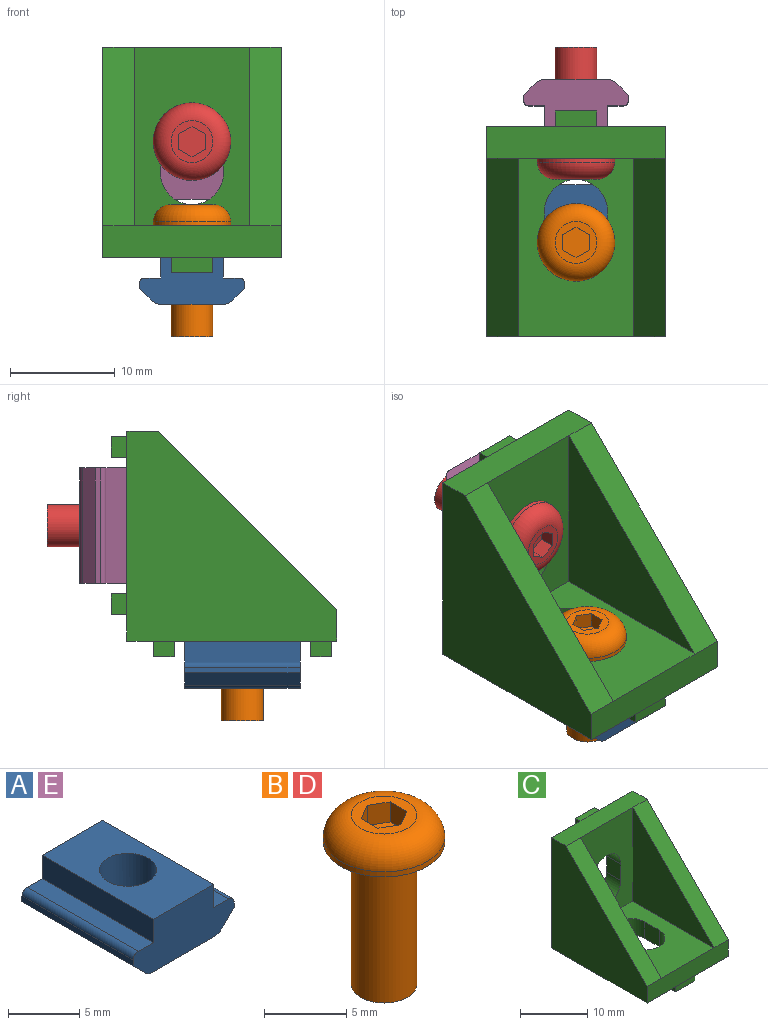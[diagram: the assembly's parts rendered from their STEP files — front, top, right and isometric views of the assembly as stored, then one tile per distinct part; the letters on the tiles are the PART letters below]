
ASSEMBLY  parts=5 mates=4
PART A: 17 faces, bbox 10x11x4.5 mm
  f0: plane 11x1.21mm, normal (-0.71,0,-0.71), area 18.8mm2, adj f1,f13,f14,f15
  f1: cylinder r=1mm len=11mm, axis (0,1,0), area 8.6mm2, adj f0,f2,f14,f15
  f2: plane 11x6.17mm, normal (0,0,-1), area 55.3mm2, adj f1,f3,f14,f15,f16
  f3: cylinder r=1mm len=11mm, axis (0,1,0), area 8.6mm2, adj f2,f4,f14,f15
  f4: plane 11x1.21mm, normal (0.71,0,-0.71), area 18.8mm2, adj f3,f5,f14,f15
  f5: plane 11x0.5mm, normal (1,0,0), area 5.5mm2, adj f4,f6,f14,f15
  f6: cylinder r=0.5mm len=11mm, axis (0,1,0), area 8.6mm2, adj f5,f7,f14,f15
  f7: plane 11x1.5mm, normal (0,0,1), area 16.5mm2, adj f6,f8,f14,f15
  f8: plane 11x2mm, normal (1,0,0), area 22mm2, adj f7,f9,f14,f15
  f9: plane 11x6mm, normal (0,0,1), area 53.4mm2, adj f8,f10,f14,f15,f16
  f10: plane 11x2mm, normal (-1,0,0), area 22mm2, adj f9,f11,f14,f15
  f11: plane 11x1.5mm, normal (0,0,1), area 16.5mm2, adj f10,f12,f14,f15
  f12: cylinder r=0.5mm len=11mm, axis (0,1,0), area 8.6mm2, adj f11,f13,f14,f15
  f13: plane 11x0.5mm, normal (-1,0,0), area 5.5mm2, adj f0,f12,f14,f15
  f14: plane 10x4.5mm, normal (0,-1,0), area 34.6mm2, adj f0,f1,f2,f3,f4,f5,f6,f7
  f15: plane 10x4.5mm, normal (0,1,0), area 34.6mm2, adj f0,f1,f2,f3,f4,f5,f6,f7
  f16: cylinder r=2mm len=4.5mm, axis (0,0,1), area 56.5mm2, adj f2,f9
PART B: 14 faces, bbox 8x8x12.6 mm
  f0: plane 4x4mm, normal (0,0,1), area 7.2mm2, adj f5,f6,f7,f8,f9,f10,f11
  f1: cylinder r=2mm len=10.4mm, axis (0,0,1), area 130.7mm2, adj f2,f13
  f2: torus R=2.2mm, axis (0,0,1), area 4.1mm2, adj f1,f3
  f3: plane 7.4x7.4mm, normal (0,0,-1), area 27.8mm2, adj f2,f4
  f4: cylinder r=3.7mm len=7.4mm, axis (0,0,1), area 8.8mm2, adj f3,f5
  f5: torus R=2mm, axis (0,0,1), area 49.9mm2, adj f0,f4
  f6: plane 1.5x1.25mm, normal (-0.5,-0.87,0), area 2.2mm2, adj f0,f7,f11,f12
  f7: plane 1.5x1.25mm, normal (0.5,-0.87,0), area 2.2mm2, adj f0,f6,f8,f12
  f8: plane 1.5x1.44mm, normal (1,0,0), area 2.2mm2, adj f0,f7,f9,f12
  f9: plane 1.5x1.25mm, normal (0.5,0.87,0), area 2.2mm2, adj f0,f8,f10,f12
  f10: plane 1.5x1.25mm, normal (-0.5,0.87,0), area 2.2mm2, adj f0,f9,f11,f12
  f11: plane 1.5x1.44mm, normal (-1,0,0), area 2.2mm2, adj f0,f6,f10,f12
  f12: plane 2.89x2.5mm, normal (0,0,1), area 5.4mm2, adj f6,f7,f8,f9,f10,f11
  f13: plane 4x4mm, normal (0,0,-1), area 12.6mm2, adj f1
PART C: 40 faces, bbox 17x21.5x21.5 mm
  f0: plane 17x11mm, normal (0,0,1), area 140.7mm2, adj f1,f3,f5,f6,f7,f8,f17,f19
  f1: plane 17x11mm, normal (0,-1,0), area 140.7mm2, adj f0,f11,f12,f13,f14,f15,f17,f19
  f2: plane 20x20mm, normal (-1,0,0), area 255.5mm2, adj f3,f9,f10,f14,f18
  f3: plane 17x3mm, normal (0,-1,0), area 51mm2, adj f0,f2,f4,f10,f16,f18
  f4: plane 20x20mm, normal (1,0,0), area 255.5mm2, adj f3,f9,f10,f14,f16
  f5: cylinder r=3mm len=6mm, axis (0,0,-1), area 28.3mm2, adj f0,f6,f8,f10
  f6: plane 3x3mm, normal (1,0,0), area 9mm2, adj f0,f5,f7,f10
  f7: cylinder r=3mm len=6mm, axis (0,0,-1), area 28.3mm2, adj f0,f6,f8,f10
  f8: plane 3x3mm, normal (-1,0,0), area 9mm2, adj f0,f5,f7,f10
  f9: plane 20x17mm, normal (0,1,0), area 277.7mm2, adj f2,f4,f10,f11,f12,f13,f14,f15
  f10: plane 20x17mm, normal (0,0,-1), area 277.7mm2, adj f2,f3,f4,f5,f6,f7,f8,f9
  f11: plane 3x3mm, normal (-1,0,0), area 9mm2, adj f1,f9,f12,f15
  f12: cylinder r=3mm len=6mm, axis (0,1,0), area 28.3mm2, adj f1,f9,f11,f13
  f13: plane 3x3mm, normal (1,0,0), area 9mm2, adj f1,f9,f12,f15
  f14: plane 17x3mm, normal (0,0,1), area 51mm2, adj f1,f2,f4,f9,f16,f18
  f15: cylinder r=3mm len=6mm, axis (0,1,0), area 28.3mm2, adj f1,f9,f11,f13
  f16: plane 17x17mm, normal (0,-0.71,0.71), area 72.1mm2, adj f3,f4,f14,f17
  f17: plane 17x17mm, normal (-1,0,0), area 144.5mm2, adj f0,f1,f16
  f18: plane 17x17mm, normal (0,-0.71,0.71), area 72.1mm2, adj f2,f3,f14,f19
  f19: plane 17x17mm, normal (1,0,0), area 144.5mm2, adj f0,f1,f18
  f20: plane 2x1.5mm, normal (-1,0,0), area 3mm2, adj f10,f21,f23,f24
  f21: plane 4x1.5mm, normal (0,-1,0), area 6mm2, adj f10,f20,f22,f24
  f22: plane 2x1.5mm, normal (1,0,0), area 3mm2, adj f10,f21,f23,f24
  f23: plane 4x1.5mm, normal (0,1,0), area 6mm2, adj f10,f20,f22,f24
  f24: plane 4x2mm, normal (0,0,-1), area 8mm2, adj f20,f21,f22,f23
  f25: plane 2x1.5mm, normal (-1,0,0), area 3mm2, adj f10,f26,f28,f29
  f26: plane 4x1.5mm, normal (0,-1,0), area 6mm2, adj f10,f25,f27,f29
  f27: plane 2x1.5mm, normal (1,0,0), area 3mm2, adj f10,f26,f28,f29
  f28: plane 4x1.5mm, normal (0,1,0), area 6mm2, adj f10,f25,f27,f29
  f29: plane 4x2mm, normal (0,0,-1), area 8mm2, adj f25,f26,f27,f28
  f30: plane 2x1.5mm, normal (-1,0,0), area 3mm2, adj f9,f31,f33,f34
  f31: plane 4x1.5mm, normal (0,0,1), area 6mm2, adj f9,f30,f32,f34
  f32: plane 2x1.5mm, normal (1,0,0), area 3mm2, adj f9,f31,f33,f34
  f33: plane 4x1.5mm, normal (0,0,-1), area 6mm2, adj f9,f30,f32,f34
  f34: plane 4x2mm, normal (0,1,0), area 8mm2, adj f30,f31,f32,f33
  f35: plane 2x1.5mm, normal (-1,0,0), area 3mm2, adj f9,f36,f38,f39
  f36: plane 4x1.5mm, normal (0,0,1), area 6mm2, adj f9,f35,f37,f39
  f37: plane 2x1.5mm, normal (1,0,0), area 3mm2, adj f9,f36,f38,f39
  f38: plane 4x1.5mm, normal (0,0,-1), area 6mm2, adj f9,f35,f37,f39
  f39: plane 4x2mm, normal (0,1,0), area 8mm2, adj f35,f36,f37,f38
PART D: same geometry as B
PART E: same geometry as A
PLACE A t=(0,-50,-5)mm
PLACE B at identity
PLACE C t=(0,-29,-5)mm
PLACE D rot(axis=(1,0,0),90deg) t=(0,-24,36)mm
PLACE E rot(axis=(1,0,0),90deg) t=(0,-19,-14)mm
MATE fastened C.f12 <-> D.f2  axis (0,-1,0) through (0,-22,6)mm
MATE fastened C.f5 <-> B.f2  axis (0,0,1) through (0,-30,-2)mm
MATE fastened E.f16 <-> C.f12  axis (0,-1,0) through (0,-19,6)mm
MATE fastened A.f16 <-> C.f5  axis (0,0,1) through (0,-30,-5)mm
